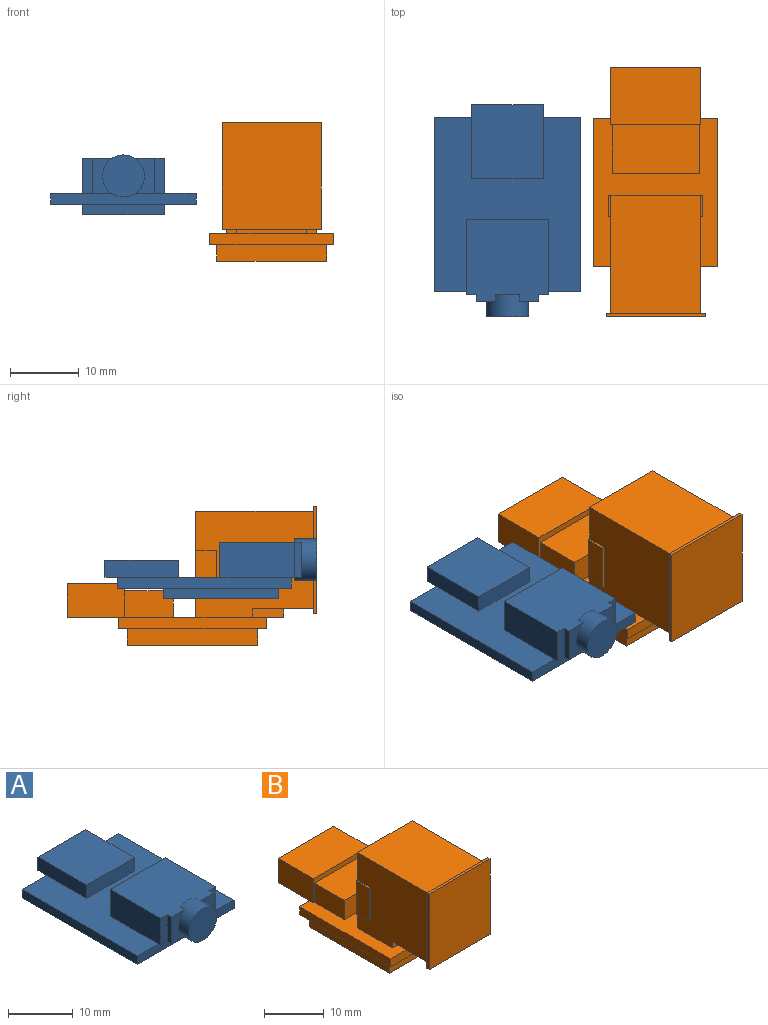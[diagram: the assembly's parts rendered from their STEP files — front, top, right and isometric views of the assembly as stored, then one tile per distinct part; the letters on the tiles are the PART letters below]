
ASSEMBLY  parts=2 mates=1
PART A: 32 faces, bbox 21.2x30.9x8.7 mm
  f0: plane 11.99x11.96mm, normal (0,0,1), area 137.4mm2, adj f1,f3,f15,f16,f17,f18,f19,f20
  f1: plane 5.11x2.88mm, normal (0,-1,0), area 9.8mm2, adj f0,f14,f21,f28
  f2: plane 25.25x21.21mm, normal (0,0,1), area 318.3mm2, adj f5,f6,f7,f8,f16,f17,f18,f23
  f3: plane 5.11x1.42mm, normal (0,-1,0), area 7.3mm2, adj f0,f14,f18,f21
  f4: plane 25.25x21.21mm, normal (0,0,-1), area 335.3mm2, adj f5,f6,f7,f8,f9,f11,f12,f13
  f5: plane 21.21x1.6mm, normal (0,1,0), area 33.9mm2, adj f2,f4,f7,f8,f22
  f6: plane 21.21x1.6mm, normal (0,-1,0), area 33.9mm2, adj f2,f4,f7,f8,f14
  f7: plane 25.25x1.6mm, normal (1,0,0), area 40.4mm2, adj f2,f4,f5,f6
  f8: plane 25.25x1.6mm, normal (-1,0,0), area 40.4mm2, adj f2,f4,f5,f6
  f9: plane 11.94x1.52mm, normal (0,-1,0), area 18.2mm2, adj f4,f10,f12,f13
  f10: plane 16.76x11.94mm, normal (0,0,-1), area 200.1mm2, adj f9,f11,f12,f13
  f11: plane 11.94x1.52mm, normal (0,1,0), area 18.2mm2, adj f4,f10,f12,f13
  f12: plane 16.76x1.52mm, normal (1,0,0), area 25.5mm2, adj f4,f9,f10,f11
  f13: plane 16.76x1.52mm, normal (-1,0,0), area 25.5mm2, adj f4,f9,f10,f11
  f14: plane 11.99x1.5mm, normal (0,0,-1), area 12mm2, adj f1,f3,f6,f15,f17,f18,f19,f20
  f15: plane 5.11x1.42mm, normal (0,-1,0), area 7.3mm2, adj f0,f14,f17,f20
  f16: plane 11.99x5.11mm, normal (0,1,0), area 61.2mm2, adj f0,f2,f17,f18
  f17: plane 11x5.11mm, normal (1,0,0), area 56.2mm2, adj f0,f2,f14,f15,f16
  f18: plane 11x5.11mm, normal (-1,0,0), area 56.2mm2, adj f0,f2,f3,f14,f16
  f19: plane 5.11x2.88mm, normal (0,-1,0), area 9.8mm2, adj f0,f14,f20,f28
  f20: plane 5.11x0.97mm, normal (1,0,0), area 4.9mm2, adj f0,f14,f15,f19
  f21: plane 5.11x0.97mm, normal (-1,0,0), area 4.9mm2, adj f0,f1,f3,f14
  f22: plane 10.44x1.88mm, normal (0,0,-1), area 19.6mm2, adj f5,f24,f26,f27
  f23: plane 10.44x2.53mm, normal (0,-1,0), area 26.4mm2, adj f2,f25,f26,f27
  f24: plane 10.44x2.53mm, normal (0,1,0), area 26.4mm2, adj f22,f25,f26,f27
  f25: plane 10.67x10.44mm, normal (0,0,1), area 111.4mm2, adj f23,f24,f26,f27
  f26: plane 10.67x2.53mm, normal (1,0,0), area 27mm2, adj f2,f22,f23,f24,f25
  f27: plane 10.67x2.53mm, normal (-1,0,0), area 27mm2, adj f2,f22,f23,f24,f25
  f28: cylinder r=3.06mm len=6.12mm, axis (0,1,0), area 50.4mm2, adj f0,f1,f14,f19,f29,f30,f31
  f29: plane 6.12x6.12mm, normal (0,-1,0), area 29.4mm2, adj f28
  f30: plane 3.38x0.51mm, normal (0,1,0), area 1.2mm2, adj f0,f28
  f31: plane 3.38x0.51mm, normal (0,1,0), area 1.2mm2, adj f14,f28
PART B: 46 faces, bbox 18x36.4x20.2 mm
  f0: plane 21.54x17.98mm, normal (0,0,-1), area 83.3mm2, adj f5,f6,f7,f8,f41,f43,f44,f45
  f1: plane 1.45x1.3mm, normal (0,-1,0), area 1.9mm2, adj f2,f4,f13,f40
  f2: plane 13.01x8.92mm, normal (0,0,-1), area 69.5mm2, adj f1,f11,f12,f13,f25,f38,f39,f40
  f3: plane 13.21x4.93mm, normal (0,-1,0), area 15.4mm2, adj f4,f30,f31,f32,f34,f35,f36
  f4: plane 21.54x17.98mm, normal (0,0,1), area 157.1mm2, adj f1,f3,f5,f6,f7,f8,f9,f11
  f5: plane 17.98x1.63mm, normal (0,-1,0), area 29.2mm2, adj f0,f4,f7,f8,f37
  f6: plane 17.98x1.63mm, normal (0,1,0), area 29.2mm2, adj f0,f4,f7,f8,f28
  f7: plane 21.54x1.63mm, normal (1,0,0), area 35mm2, adj f0,f4,f5,f6
  f8: plane 21.54x1.63mm, normal (-1,0,0), area 35mm2, adj f0,f4,f5,f6
  f9: plane 15.47x13.61mm, normal (0,1,0), area 205.3mm2, adj f4,f10,f12,f13,f14,f16,f17,f19
  f10: plane 17.17x13.01mm, normal (0,0,1), area 223.3mm2, adj f9,f12,f13,f25
  f11: plane 1.45x1.3mm, normal (0,-1,0), area 1.9mm2, adj f2,f4,f12,f39
  f12: plane 17.17x15.47mm, normal (1,0,0), area 233.1mm2, adj f2,f4,f9,f10,f11,f14,f15,f16
  f13: plane 17.17x15.47mm, normal (-1,0,0), area 233.1mm2, adj f1,f2,f4,f9,f10,f17,f18,f19
  f14: plane 3.05x0.31mm, normal (0,0,-1), area 0.9mm2, adj f9,f12,f15,f20
  f15: plane 6.86x0.31mm, normal (0,-1,0), area 2.1mm2, adj f12,f14,f16,f20
  f16: plane 3.05x0.31mm, normal (0,0,1), area 0.9mm2, adj f9,f12,f15,f20
  f17: plane 3.05x0.31mm, normal (0,0,1), area 0.9mm2, adj f9,f13,f18,f21
  f18: plane 6.86x0.31mm, normal (0,-1,0), area 2.1mm2, adj f13,f17,f19,f21
  f19: plane 3.05x0.31mm, normal (0,0,-1), area 0.9mm2, adj f9,f13,f18,f21
  f20: plane 6.86x3.05mm, normal (1,0,0), area 20.9mm2, adj f9,f14,f15,f16
  f21: plane 6.86x3.05mm, normal (-1,0,0), area 20.9mm2, adj f9,f17,f18,f19
  f22: plane 14.43x0.51mm, normal (0,0,1), area 7.3mm2, adj f23,f25,f26,f27
  f23: plane 15.49x14.43mm, normal (0,-1,0), area 223.5mm2, adj f22,f24,f26,f27
  f24: plane 14.43x0.51mm, normal (0,0,-1), area 7.3mm2, adj f23,f25,f26,f27
  f25: plane 15.49x14.43mm, normal (0,1,0), area 39.2mm2, adj f2,f10,f12,f13,f22,f24,f26,f27
  f26: plane 15.49x0.51mm, normal (1,0,0), area 7.9mm2, adj f22,f23,f24,f25
  f27: plane 15.49x0.51mm, normal (-1,0,0), area 7.9mm2, adj f22,f23,f24,f25
  f28: plane 13.21x7.49mm, normal (0,0,-1), area 99mm2, adj f6,f29,f31,f32
  f29: plane 13.21x4.93mm, normal (0,1,0), area 65.1mm2, adj f28,f30,f31,f32
  f30: plane 13.21x8.38mm, normal (0,0,1), area 110.7mm2, adj f3,f29,f31,f32
  f31: plane 8.38x4.93mm, normal (1,0,0), area 41.3mm2, adj f3,f4,f28,f29,f30
  f32: plane 8.38x4.93mm, normal (-1,0,0), area 41.3mm2, adj f3,f4,f28,f29,f30
  f33: plane 12.7x3.91mm, normal (0,-1,0), area 49.7mm2, adj f4,f34,f35,f36
  f34: plane 12.7x7.11mm, normal (0,0,1), area 90.3mm2, adj f3,f33,f35,f36
  f35: plane 7.11x3.91mm, normal (1,0,0), area 27.8mm2, adj f3,f4,f33,f34
  f36: plane 7.11x3.91mm, normal (-1,0,0), area 27.8mm2, adj f3,f4,f33,f34
  f37: plane 10.11x2.54mm, normal (0,0,-1), area 25.7mm2, adj f5,f38,f39,f40
  f38: plane 10.11x1.3mm, normal (0,-1,0), area 13.1mm2, adj f2,f37,f39,f40
  f39: plane 4.6x1.3mm, normal (1,0,0), area 6mm2, adj f2,f4,f11,f37,f38
  f40: plane 4.6x1.3mm, normal (-1,0,0), area 6mm2, adj f1,f2,f4,f37,f38
  f41: plane 16x2.41mm, normal (0,-1,0), area 38.6mm2, adj f0,f42,f44,f45
  f42: plane 19x16mm, normal (0,0,-1), area 304mm2, adj f41,f43,f44,f45
  f43: plane 16x2.41mm, normal (0,1,0), area 38.6mm2, adj f0,f42,f44,f45
  f44: plane 19x2.41mm, normal (1,0,0), area 45.8mm2, adj f0,f41,f42,f43
  f45: plane 19x2.41mm, normal (-1,0,0), area 45.8mm2, adj f0,f41,f42,f43
PLACE A t=(0,3.76,-2.55)mm
PLACE B t=(21.59,7.37,-8.38)mm
MATE parallel B.f23 <-> A.f28  axis (0,-1,0) through (21.59,0,0)mm
